# Revit family: Air Source 25-185
name_source: partatom
category: Mechanical Equipment
revit_build: Autodesk Revit 2017 (Build: 20190507_1515(x64)
units: mm (PartAtom-declared; Revit-internal decimal feet)

## family parameters
Always vertical = Yes
Cut with Voids When Loaded = No
Part Type = Normal
Room Calculation Point = No
Round Connector Dimension = Use Diameter
Shared = No
Work Plane-Based = No

## types (10) — shared parameters
CONDENSATE CONN SIZE = 1"
Clearance Back = 24"
Clearance Front = 36"
Clearance Left = 24"
Clearance Right = 24"
Compressor Type = Scroll
Description = Air Source Heat Pump Water Heater
Manufacturer = Lochinvar
SES BIM Studio # = 21 0649 02
URL = https://www.lochinvar.com

## per-type parameters (varying)
- 025 Axial: 208V-230V/1PH/60HZ MCA=24; 208V-230V/1PH/60HZ MOCP=25; 208V-230V/1PH/60HZ RLA=19.7; 208V-230V/3PH/60HZ MCA=14; 208V-230V/3PH/60HZ MOCP=15; 208V-230V/3PH/60HZ RLA=11.5; 440V-480V/3PH/60HZ MCA=8; 440V-480V/3PH/60HZ MOCP=10; 440V-480V/3PH/60HZ RLA=6.5; 575V/3PH/60HZ MCA=8; 575V/3PH/60HZ MOCP=10; 575V/3PH/60HZ RLA=6.2; Air Volume (CFM)=1,250; BTUH Cooling=21,200; BTUH Heating=27,450; Blower=No; Blower Bottom from Bottom=10 7/8"; Blower Height=11 1/2"; Blower Left from Left=10 1/4"; Blower Width=7"; Center Channels=No; Channel Height=2 1/2"; Channel Length=6"; Condensate from Front=27 1/2"; Condensate from Left=15 3/8"; Controls Cover Bottom from Bottom=14 5/8"; Controls Cover Right from Right=9 25/32"; Elec Panel Bottom from Bottom=4 3/4"; Elec Panel Left from Right=22 9/16"; Elec Panel Right from Right=2"; Elec Panel Top from Bottom=24 5/8"; Evap Depth=1"; Evap Left from Left=27 1/8"; Evap Right from Left=3"; Evap Top from Bottom=22 3/4"; FLOW RATE (GPM)=5.4; Fan=Yes; Fan Center from Bottom=14 13/16"; Fan Center from Left=12 5/8"; Fan Inner Dia=18 1/2"; Fan Outer Dia=20 1/8"; Fan/Blower Depth=3"; Lbs.R134a=7; Perp Channel Center from Left=21 3/16"; Perp Channel Left from Left=3"; Perp Channel Right from Left=43 7/8"; Perpendicular Channels=No; Side Channels=Yes; UNIT HEIGHT=24 7/8"; UNIT LENGTH=45 3/8"; UNIT WIDTH=33"; Unit Top Panel Depth=1/2"; WATER CONN SIZE=1"; WEIGHT=310; Water In from Bottom=9 1/4"; Water Out from Bottom=17 1/4"; Water from Left=41"
- 025 Blower: 208V-230V/1PH/60HZ MCA=28; 208V-230V/1PH/60HZ MOCP=30; 208V-230V/1PH/60HZ RLA=23.9; 208V-230V/3PH/60HZ MCA=17; 208V-230V/3PH/60HZ MOCP=20; 208V-230V/3PH/60HZ RLA=14.4; 440V-480V/3PH/60HZ MCA=10; 440V-480V/3PH/60HZ MOCP=15; 440V-480V/3PH/60HZ RLA=7.9; 575V/3PH/60HZ MCA=8; 575V/3PH/60HZ MOCP=10; 575V/3PH/60HZ RLA=6.4; Air Volume (CFM)=1,250; BTUH Cooling=21,200; BTUH Heating=27,450; Blower=Yes; Blower Bottom from Bottom=10 7/8"; Blower Height=11 1/2"; Blower Left from Left=10 1/4"; Blower Width=7"; Center Channels=No; Channel Height=2 1/2"; Channel Length=6"; Condensate from Front=27 1/2"; Condensate from Left=15 3/8"; Controls Cover Bottom from Bottom=14 5/8"; Controls Cover Right from Right=9 25/32"; Elec Panel Bottom from Bottom=4 3/4"; Elec Panel Left from Right=22 9/16"; Elec Panel Right from Right=2"; Elec Panel Top from Bottom=24 5/8"; Evap Depth=1"; Evap Left from Left=27 1/8"; Evap Right from Left=3"; Evap Top from Bottom=22 3/4"; FLOW RATE (GPM)=5.4; Fan=No; Fan Center from Bottom=14 13/16"; Fan Center from Left=12 5/8"; Fan Inner Dia=18 1/2"; Fan Outer Dia=20 1/8"; Fan/Blower Depth=1 3/8"; Lbs.R134a=7; Model=AHP025; Perp Channel Center from Left=21 3/16"; Perp Channel Left from Left=3"; Perp Channel Right from Left=43 7/8"; Perpendicular Channels=No; Side Channels=Yes; UNIT HEIGHT=24 7/8"; UNIT LENGTH=45 3/8"; UNIT WIDTH=31 3/8"; Unit Top Panel Depth=1/2"; WATER CONN SIZE=1"; WEIGHT=310; Water In from Bottom=9 1/4"; Water Out from Bottom=17 1/4"; Water from Left=41"
- 060 Axial: 208V-230V/1PH/60HZ MCA=41; 208V-230V/1PH/60HZ MOCP=50; 208V-230V/1PH/60HZ RLA=33.1; 208V-230V/3PH/60HZ MCA=29; 208V-230V/3PH/60HZ MOCP=30; 208V-230V/3PH/60HZ RLA=25; 440V-480V/3PH/60HZ MCA=15; 440V-480V/3PH/60HZ MOCP=20; 440V-480V/3PH/60HZ RLA=12; 575V/3PH/60HZ MCA=12; 575V/3PH/60HZ MOCP=15; 575V/3PH/60HZ RLA=10; Air Volume (CFM)=2,800; BTUH Cooling=48,425; BTUH Heating=63,255; Blower=No; Blower Bottom from Bottom=10 7/8"; Blower Height=11 1/2"; Blower Left from Left=10 1/4"; Blower Width=7"; Center Channels=No; Channel Height=2 1/2"; Channel Length=6"; Condensate from Front=25 5/8"; Condensate from Left=22 3/4"; Controls Cover Bottom from Bottom=20 1/4"; Controls Cover Right from Right=17 13/16"; Elec Panel Bottom from Bottom=4 7/8"; Elec Panel Left from Right=32 5/8"; Elec Panel Right from Right=8"; Elec Panel Top from Bottom=28"; Evap Depth=1"; Evap Left from Left=41 3/8"; Evap Right from Left=5 1/4"; Evap Top from Bottom=30 1/4"; FLOW RATE (GPM)=13; Fan=Yes; Fan Center from Bottom=19 1/2"; Fan Center from Left=17"; Fan Inner Dia=27 5/8"; Fan Outer Dia=29 1/4"; Fan/Blower Depth=4"; Lbs.R134a=14; Model=AHP060; Perp Channel Center from Left=21 3/16"; Perp Channel Left from Left=3"; Perp Channel Right from Left=43 7/8"; Perpendicular Channels=No; Side Channels=Yes; UNIT HEIGHT=34 5/8"; UNIT LENGTH=64 1/4"; UNIT WIDTH=32 5/8"; Unit Top Panel Depth=1"; WATER CONN SIZE=1"; WEIGHT=520; Water In from Bottom=7 1/2"; Water Out from Bottom=17 1/2"; Water from Left=58 3/8"
- 060 Blower: 208V-230V/1PH/60HZ MCA=44; 208V-230V/1PH/60HZ MOCP=50; 208V-230V/1PH/60HZ RLA=36.3; 208V-230V/3PH/60HZ MCA=32; 208V-230V/3PH/60HZ MOCP=35; 208V-230V/3PH/60HZ RLA=26.5; 440V-480V/3PH/60HZ MCA=16; 440V-480V/3PH/60HZ MOCP=20; 440V-480V/3PH/60HZ RLA=13.2; 575V/3PH/60HZ MCA=13; 575V/3PH/60HZ MOCP=15; 575V/3PH/60HZ RLA=10.8; Air Volume (CFM)=2,800; BTUH Cooling=48,425; BTUH Heating=63,255; Blower=Yes; Blower Bottom from Bottom=19 3/4"; Blower Height=13 3/4"; Blower Left from Left=14"; Blower Width=16 1/8"; Center Channels=No; Channel Height=2 1/2"; Channel Length=6"; Condensate from Front=25 5/8"; Condensate from Left=22 3/4"; Controls Cover Bottom from Bottom=20 1/4"; Controls Cover Right from Right=17 13/16"; Elec Panel Bottom from Bottom=4 7/8"; Elec Panel Left from Right=32 5/8"; Elec Panel Right from Right=8"; Elec Panel Top from Bottom=28"; Evap Depth=1"; Evap Left from Left=41 3/8"; Evap Right from Left=5 1/4"; Evap Top from Bottom=30 1/4"; FLOW RATE (GPM)=13; Fan=No; Fan Center from Bottom=19 1/2"; Fan Center from Left=17"; Fan Inner Dia=27 5/8"; Fan Outer Dia=29 1/4"; Fan/Blower Depth=1 1/8"; Lbs.R134a=14; Model=AHP060; Perp Channel Center from Left=21 3/16"; Perp Channel Left from Left=3"; Perp Channel Right from Left=43 7/8"; Perpendicular Channels=No; Side Channels=Yes; UNIT HEIGHT=34 5/8"; UNIT LENGTH=64 1/4"; UNIT WIDTH=29 5/8"; Unit Top Panel Depth=1"; WATER CONN SIZE=1"; WEIGHT=520; Water In from Bottom=7 1/2"; Water Out from Bottom=17 1/2"; Water from Left=58 3/8"
- 090 Axial: 208V-230V/1PH/60HZ MCA=-; 208V-230V/1PH/60HZ MOCP=-; 208V-230V/1PH/60HZ RLA=-; 208V-230V/3PH/60HZ MCA=49; 208V-230V/3PH/60HZ MOCP=50; 208V-230V/3PH/60HZ RLA=39.3; 440V-480V/3PH/60HZ MCA=26; 440V-480V/3PH/60HZ MOCP=30; 440V-480V/3PH/60HZ RLA=20.8; 575V/3PH/60HZ MCA=18; 575V/3PH/60HZ MOCP=20; 575V/3PH/60HZ RLA=14.4; Air Volume (CFM)=2,800; BTUH Cooling=83,625; BTUH Heating=110,725; Blower=No; Blower Bottom from Bottom=10 7/8"; Blower Height=11 1/2"; Blower Left from Left=10 1/4"; Blower Width=7"; Center Channels=Yes; Channel Height=3"; Channel Length=10"; Condensate from Front=24 3/4"; Condensate from Left=24 7/8"; Controls Cover Bottom from Bottom=28"; Controls Cover Right from Right=24 1/16"; Elec Panel Bottom from Bottom=5 1/2"; Elec Panel Left from Right=36 5/8"; Elec Panel Right from Right=16 1/2"; Elec Panel Top from Bottom=35 1/4"; Evap Depth=1"; Evap Left from Left=47 1/8"; Evap Right from Left=5 1/8"; Evap Top from Bottom=36 3/4"; FLOW RATE (GPM)=20; Fan=Yes; Fan Center from Bottom=20 3/8"; Fan Center from Left=18 3/4"; Fan Inner Dia=28 1/8"; Fan Outer Dia=29 3/4"; Fan/Blower Depth=4 1/8"; Lbs.R134a=21; Model=AHP090; Perp Channel Center from Left=21 3/16"; Perp Channel Left from Left=3"; Perp Channel Right from Left=43 7/8"; Perpendicular Channels=No; Side Channels=Yes; UNIT HEIGHT=40 1/4"; UNIT LENGTH=70 1/4"; UNIT WIDTH=32 3/4"; Unit Top Panel Depth=1"; WATER CONN SIZE=1 1/2"; WEIGHT=775; Water In from Bottom=8 1/4"; Water Out from Bottom=23 1/8"; Water from Left=63 1/2"
- 090 Blower: 208V-230V/1PH/60HZ MCA=-; 208V-230V/1PH/60HZ MOCP=-; 208V-230V/1PH/60HZ RLA=-; 208V-230V/3PH/60HZ MCA=51; 208V-230V/3PH/60HZ MOCP=60; 208V-230V/3PH/60HZ RLA=41.6; 440V-480V/3PH/60HZ MCA=27; 440V-480V/3PH/60HZ MOCP=30; 440V-480V/3PH/60HZ RLA=22; 575V/3PH/60HZ MCA=19; 575V/3PH/60HZ MOCP=20; 575V/3PH/60HZ RLA=15.2; Air Volume (CFM)=2,800; BTUH Cooling=83,625; BTUH Heating=110,725; Blower=Yes; Blower Bottom from Bottom=19 1/2"; Blower Height=13 3/4"; Blower Left from Left=16 1/4"; Blower Width=15 3/4"; Center Channels=Yes; Channel Height=3"; Channel Length=10"; Condensate from Front=24 3/4"; Condensate from Left=24 7/8"; Controls Cover Bottom from Bottom=28"; Controls Cover Right from Right=24 1/16"; Elec Panel Bottom from Bottom=5 1/2"; Elec Panel Left from Right=36 5/8"; Elec Panel Right from Right=16 1/2"; Elec Panel Top from Bottom=35 1/4"; Evap Depth=1"; Evap Left from Left=47 1/8"; Evap Right from Left=5 1/8"; Evap Top from Bottom=36 3/4"; FLOW RATE (GPM)=20; Fan=No; Fan Center from Bottom=20 3/8"; Fan Center from Left=18 3/4"; Fan Inner Dia=28 1/8"; Fan Outer Dia=29 3/4"; Fan/Blower Depth=1 1/4"; Lbs.R134a=21; Model=AHP090; Perp Channel Center from Left=21 3/16"; Perp Channel Left from Left=3"; Perp Channel Right from Left=43 7/8"; Perpendicular Channels=No; Side Channels=Yes; UNIT HEIGHT=40 1/4"; UNIT LENGTH=70 1/4"; UNIT WIDTH=29 3/4"; Unit Top Panel Depth=1"; WATER CONN SIZE=1 1/2"; WEIGHT=775; Water In from Bottom=8 1/4"; Water Out from Bottom=23 1/8"; Water from Left=63 1/2"
- 125 Axial: 208V-230V/1PH/60HZ MCA=-; 208V-230V/1PH/60HZ MOCP=-; 208V-230V/1PH/60HZ RLA=-; 208V-230V/3PH/60HZ MCA=69; 208V-230V/3PH/60HZ MOCP=70; 208V-230V/3PH/60HZ RLA=56.3; 440V-480V/3PH/60HZ MCA=34; 440V-480V/3PH/60HZ MOCP=35; 440V-480V/3PH/60HZ RLA=28.2; 575V/3PH/60HZ MCA=30; 575V/3PH/60HZ MOCP=35; 575V/3PH/60HZ RLA=24.7; Air Volume (CFM)=4,500; BTUH Cooling=108,500; BTUH Heating=114,275; Blower=No; Blower Bottom from Bottom=10 7/8"; Blower Height=11 1/2"; Blower Left from Left=10 1/4"; Blower Width=7"; Center Channels=No; Channel Height=3"; Channel Length=10"; Condensate from Front=28 5/8"; Condensate from Left=36"; Controls Cover Bottom from Bottom=22 3/4"; Controls Cover Right from Right=24 11/16"; Elec Panel Bottom from Bottom=6 1/8"; Elec Panel Left from Right=40 1/8"; Elec Panel Right from Right=14 1/4"; Elec Panel Top from Bottom=30 5/8"; Evap Depth=1"; Evap Left from Left=65 3/8"; Evap Right from Left=5 3/8"; Evap Top from Bottom=31 3/4"; FLOW RATE (GPM)=28; Fan=Yes; Fan Center from Bottom=20 5/8"; Fan Center from Left=29 3/4"; Fan Inner Dia=27 3/8"; Fan Outer Dia=29"; Fan/Blower Depth=4 1/8"; Lbs.R134a=25; Model=AHP125; Perp Channel Center from Left=42 15/16"; Perp Channel Left from Left=3"; Perp Channel Right from Left=82 7/8"; Perpendicular Channels=Yes; Side Channels=No; UNIT HEIGHT=36 1/8"; UNIT LENGTH=84 3/8"; UNIT WIDTH=37 3/8"; Unit Top Panel Depth=1"; WATER CONN SIZE=1 1/2"; WEIGHT=1,240; Water In from Bottom=9 1/8"; Water Out from Bottom=29 1/8"; Water from Left=75"
- 125 Blower: 208V-230V/1PH/60HZ MCA=-; 208V-230V/1PH/60HZ MOCP=-; 208V-230V/1PH/60HZ RLA=-; 208V-230V/3PH/60HZ MCA=74; 208V-230V/3PH/60HZ MOCP=80; 208V-230V/3PH/60HZ RLA=61.4; 440V-480V/3PH/60HZ MCA=37; 440V-480V/3PH/60HZ MOCP=40; 440V-480V/3PH/60HZ RLA=30.9; 575V/3PH/60HZ MCA=32; 575V/3PH/60HZ MOCP=35; 575V/3PH/60HZ RLA=26.8; Air Volume (CFM)=4,500; BTUH Cooling=108,500; BTUH Heating=114,275; Blower=Yes; Blower Bottom from Bottom=17 3/8"; Blower Height=16 1/2"; Blower Left from Left=20 5/8"; Blower Width=18 7/8"; Center Channels=No; Channel Height=3"; Channel Length=10"; Condensate from Front=28 5/8"; Condensate from Left=36"; Controls Cover Bottom from Bottom=22 3/4"; Controls Cover Right from Right=24 11/16"; Elec Panel Bottom from Bottom=6 1/8"; Elec Panel Left from Right=40 1/8"; Elec Panel Right from Right=14 1/4"; Elec Panel Top from Bottom=30 5/8"; Evap Depth=1"; Evap Left from Left=65 3/8"; Evap Right from Left=5 3/8"; Evap Top from Bottom=31 3/4"; FLOW RATE (GPM)=28; Fan=No; Fan Center from Bottom=20 5/8"; Fan Center from Left=29 3/4"; Fan Inner Dia=27 3/8"; Fan Outer Dia=29"; Fan/Blower Depth=1 1/8"; Lbs.R134a=25; Model=AHP125; Perp Channel Center from Left=42 15/16"; Perp Channel Left from Left=3"; Perp Channel Right from Left=82 7/8"; Perpendicular Channels=Yes; Side Channels=No; UNIT HEIGHT=36 1/8"; UNIT LENGTH=84 3/8"; UNIT WIDTH=34 3/8"; Unit Top Panel Depth=1"; WATER CONN SIZE=1 1/2"; WEIGHT=1,240; Water In from Bottom=9 1/8"; Water Out from Bottom=29 1/8"; Water from Left=75"
- 185 Axial: 208V-230V/1PH/60HZ MCA=-; 208V-230V/1PH/60HZ MOCP=-; 208V-230V/1PH/60HZ RLA=-; 208V-230V/3PH/60HZ MCA=100; 208V-230V/3PH/60HZ MOCP=110; 208V-230V/3PH/60HZ RLA=81.3; 440V-480V/3PH/60HZ MCA=45; 440V-480V/3PH/60HZ MOCP=50; 440V-480V/3PH/60HZ RLA=36.5; 575V/3PH/60HZ MCA=37; 575V/3PH/60HZ MOCP=40; 575V/3PH/60HZ RLA=30.5; Air Volume (CFM)=4,500; BTUH Cooling=172,375; BTUH Heating=224,675; Blower=No; Blower Bottom from Bottom=10 7/8"; Blower Height=11 1/2"; Blower Left from Left=10 1/4"; Blower Width=7"; Center Channels=No; Channel Height=3"; Channel Length=10"; Condensate from Front=37 1/2"; Condensate from Left=26 3/8"; Controls Cover Bottom from Bottom=28 3/4"; Controls Cover Right from Right=42 3/8"; Elec Panel Bottom from Bottom=6 1/8"; Elec Panel Left from Right=56 7/8"; Elec Panel Right from Right=32 7/8"; Elec Panel Top from Bottom=37"; Evap Depth=1 1/4"; Evap Left from Left=67 1/8"; Evap Right from Left=19 1/8"; Evap Top from Bottom=41 1/2"; FLOW RATE (GPM)=40; Fan=Yes; Fan Center from Bottom=21 9/16"; Fan Center from Left=55 5/16"; Fan Inner Dia=29 1/4"; Fan Outer Dia=30 7/8"; Fan/Blower Depth=3 3/4"; Lbs.R134a=30; Model=AHP185; Perp Channel Center from Left=21 1/4"; Perp Channel Left from Left=1 1/2"; Perp Channel Right from Left=72 3/4"; Perpendicular Channels=Yes; Side Channels=No; UNIT HEIGHT=43"; UNIT LENGTH=72 3/4"; UNIT WIDTH=45 3/8"; Unit Top Panel Depth=1"; WATER CONN SIZE=2"; WEIGHT=1,410; Water In from Bottom=11 5/8"; Water Out from Bottom=38 1/8"; Water from Left=11 1/2"
- 185 Blower: 208V-230V/1PH/60HZ MCA=-; 208V-230V/1PH/60HZ MOCP=-; 208V-230V/1PH/60HZ RLA=-; 208V-230V/3PH/60HZ MCA=105; 208V-230V/3PH/60HZ MOCP=110; 208V-230V/3PH/60HZ RLA=86.4; 440V-480V/3PH/60HZ MCA=47; 440V-480V/3PH/60HZ MOCP=50; 440V-480V/3PH/60HZ RLA=39.2; 575V/3PH/60HZ MCA=39; 575V/3PH/60HZ MOCP=40; 575V/3PH/60HZ RLA=32.6; Air Volume (CFM)=4,500; BTUH Cooling=172,375; BTUH Heating=224,675; Blower=Yes; Blower Bottom from Bottom=18 1/4"; Blower Height=16"; Blower Left from Left=44 3/4"; Blower Width=19"; Center Channels=No; Channel Height=3"; Channel Length=10"; Condensate from Front=37 1/2"; Condensate from Left=26 3/8"; Controls Cover Bottom from Bottom=28 3/4"; Controls Cover Right from Right=42 3/8"; Elec Panel Bottom from Bottom=6 1/8"; Elec Panel Left from Right=56 7/8"; Elec Panel Right from Right=32 7/8"; Elec Panel Top from Bottom=37"; Evap Depth=1 1/4"; Evap Left from Left=67 1/8"; Evap Right from Left=19 1/8"; Evap Top from Bottom=41 1/2"; FLOW RATE (GPM)=40; Fan=No; Fan Center from Bottom=21 9/16"; Fan Center from Left=55 5/16"; Fan Inner Dia=29 1/4"; Fan Outer Dia=30 7/8"; Fan/Blower Depth=1 1/8"; Lbs.R134a=30; Model=AHP185; Perp Channel Center from Left=21 1/4"; Perp Channel Left from Left=1 1/2"; Perp Channel Right from Left=72 3/4"; Perpendicular Channels=Yes; Side Channels=No; UNIT HEIGHT=43"; UNIT LENGTH=72 3/4"; UNIT WIDTH=42 3/4"; Unit Top Panel Depth=1"; WATER CONN SIZE=2"; WEIGHT=1,410; Water In from Bottom=11 5/8"; Water Out from Bottom=38 1/8"; Water from Left=11 1/2"

## geometry (parser evidence)
native form markers: Sweep x1
no freeform markers — native parametric forms only
